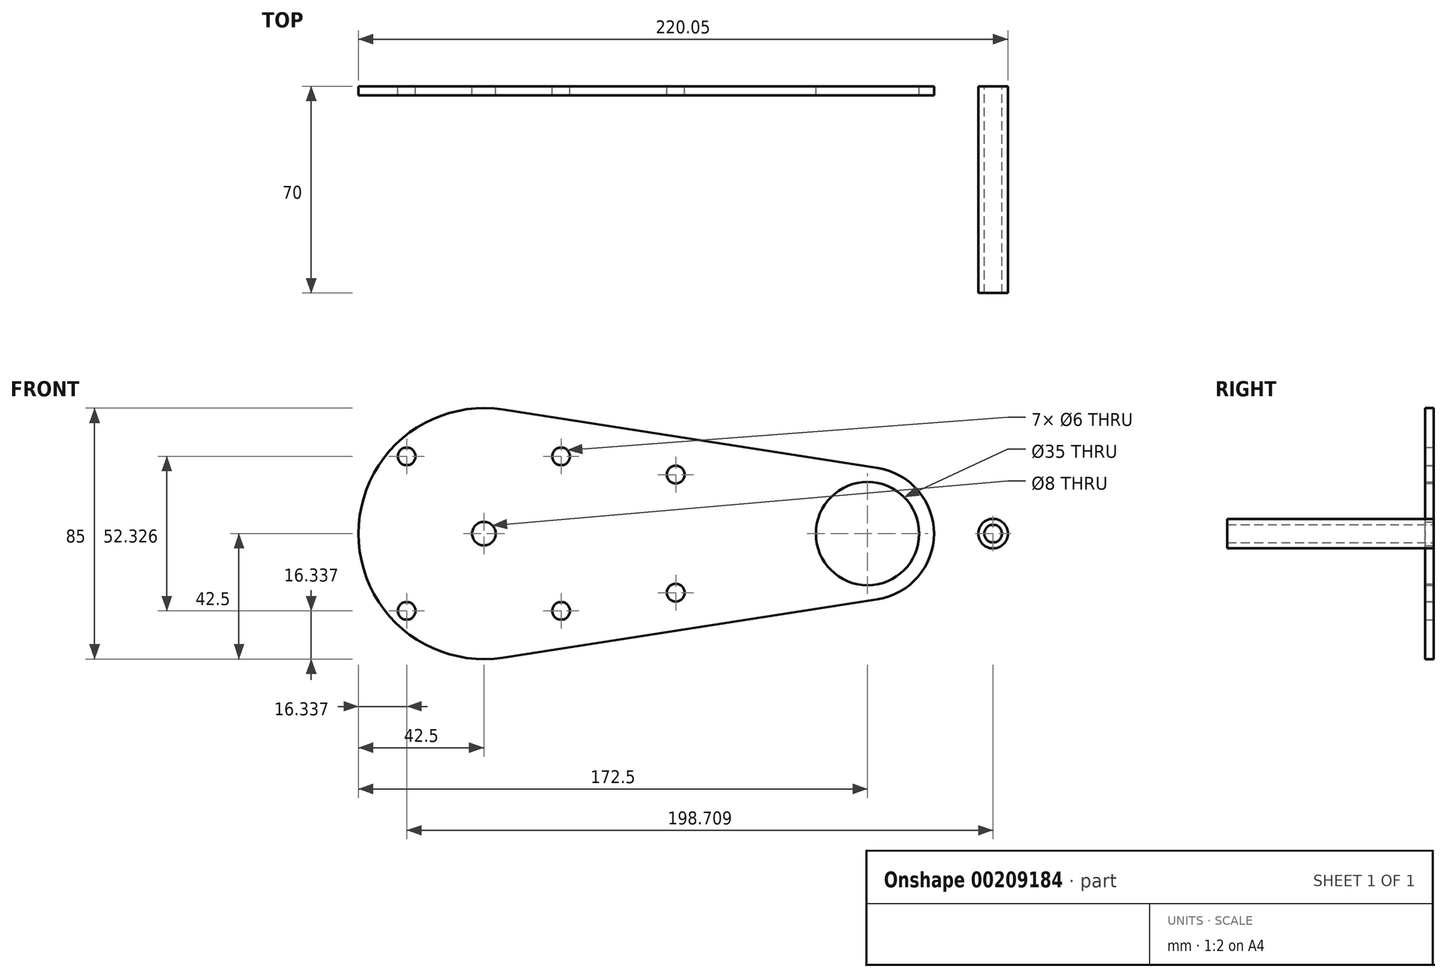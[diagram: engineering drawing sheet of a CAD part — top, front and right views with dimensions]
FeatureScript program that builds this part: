
annotation { "Feature Type Name" : "Feature", "Feature Type Description" : "" }
export const myFeature = defineFeature(function(context is Context, id is Id, definition is map)
    precondition{}
    {
        {
            var Q0;
            Q0=qCreatedBy(makeId("Front.planeOp"),FACE);
            var sketch = newSketch(context, id + "F0", { "sketchPlane" : qUnion([Q0])});
            skCircle(sketch, "E0", {"center": v(0, 0) * mm, "radius": 17.5 * mm});
            skCircle(sketch, "E1", {"center": v(0, 0) * mm, "radius": 22.5 * mm});
            skLineSegment(sketch, "E2", {"start": v(0, 0) * mm, "end": v(-130, 0) * mm, "construction": true});
            skCircle(sketch, "E3", {"center": v(-130, 0) * mm, "radius": 42.5 * mm});
            skCircle(sketch, "E4", {"center": v(-130, 0) * mm, "radius": 4 * mm});
            skLineSegment(sketch, "E5", {"start": v(3.46, -22.23) * mm, "end": v(-123.46, -42) * mm});
            skLineSegment(sketch, "E6", {"start": v(3.46, 22.23) * mm, "end": v(-123.46, 42) * mm});
            skLineSegment(sketch, "E7", {"start": v(-130, 0) * mm, "end": v(-103.84, 26.16) * mm, "construction": true});
            skLineSegment(sketch, "E8", {"start": v(-130, 0) * mm, "end": v(-156.16, 26.16) * mm, "construction": true});
            skLineSegment(sketch, "E9", {"start": v(-130, 0) * mm, "end": v(-156.16, -26.16) * mm, "construction": true});
            skLineSegment(sketch, "E10", {"start": v(-130, 0) * mm, "end": v(-103.84, -26.16) * mm, "construction": true});
            skCircle(sketch, "E11", {"center": v(-156.16, 26.16) * mm, "radius": 3 * mm});
            skCircle(sketch, "E12", {"center": v(-103.84, 26.16) * mm, "radius": 3 * mm});
            skCircle(sketch, "E13", {"center": v(-103.84, -26.16) * mm, "radius": 3 * mm});
            skCircle(sketch, "E14", {"center": v(-156.16, -26.16) * mm, "radius": 3 * mm});
            skLineSegment(sketch, "E15", {"start": v(-65, 20) * mm, "end": v(-65, 0) * mm, "construction": true});
            skLineSegment(sketch, "E16", {"start": v(-65, -20) * mm, "end": v(-65, 0) * mm, "construction": true});
            skCircle(sketch, "E17", {"center": v(-65, 20) * mm, "radius": 3 * mm});
            skCircle(sketch, "E18", {"center": v(-65, -20) * mm, "radius": 3 * mm});
            skSolve(sketch);
        }
        {
            var Q0;
            Q0 = qSketchRegion(id + "F0", true);
            extrude(context, id + "F1", {"entities" : qUnion([Q0]), "depth" : 3 * mm});
        }
        {
            var Q0;
            Q0=qCreatedBy(makeId("Front.planeOp"),FACE);
            var sketch = newSketch(context, id + "F2", { "sketchPlane" : qUnion([Q0])});
            skCircle(sketch, "E19", {"center": v(42.55, 0) * mm, "radius": 5 * mm});
            skCircle(sketch, "E20", {"center": v(42.55, 0) * mm, "radius": 3 * mm});
            skSolve(sketch);
        }
        {
            var Q0;
            Q0=makeQuery(id+"F2.imprint","IMPRINT",FACE,{"disambiguationData":[TD([[makeQuery(id+"F2.imprint","IMPRINT",EDGE,{"derivedFrom":sQuery(id+"F2.wireOp",EDGE,"E19")}),1.0]])]});
            extrude(context, id + "F3", {"entities" : qUnion([Q0]), "depth" : 70 * mm});
        }
    });
